# Revit family: LEGRAND_NON INTERLOCKED SOCKETS_SURFACE MOUNTED_IP44_440
name_source: partatom
category: Installations électriques
revit_build: Autodesk Revit 2018 (Build: 20170223_1515(x64)
units: mm (PartAtom-declared; Revit-internal decimal feet)

## family parameters
Conserver l'orientation des annotations = Non
Cote de connecteur circulaire = Utiliser le diamètre
Couper avec des vides une fois chargée = Non
Hôte = Face
Partagée = Non
Point de calcul de pièce = Non
Type d'élément = Normal

## types (6) — shared parameters
Description = international standard socket for flush or surface mounting with accessory allows the connection of power devices
Dia bouchon = 50 mm  [stored 0.164042 ft]
Elévation par défaut = 1000 mm  [stored 3.28084 ft]
Fabricant = Legrand
Flush E or Surface mounting S = flush and surface mounting
General Conditions of Use = https://export.legrand.com
Maximum installation temperature = 40°C
Maximum use temperature = 100°C
Minimum installation temperature = -20°C
Minimum use temperature = -50°C
Number of poles = 4
RAY BOUCHON = 25 mm  [stored 0.082021 ft]
Ray = 25 mm  [stored 0.082021 ft]
Standard IEC or NFC = IEC
Tension V = 400 440 V  50 60 Hz red
characteristic color = red
connecting type = screw terminals
material of box = plastic
resistance to chocks IK = 09
vertical fixing distance mm = 70 mm

## per-type parameters (varying)
| type | Modèle | Position of earth h | depth for flush mounting mm | depth mm | h1 | halogen free | height mm | horizontal fixing distance mm | intensity A | protection class IP | width mm |
| panel mounting socket Hypra   IP 44   ELV 16 A   440/460 V   2P+E   plast surface box for passage wiring | 052310 | 11 | 75 mm | 115 mm | 109 mm | Oui | 182 mm | 60 mm | 16 A | IP44 | 86 mm |
| panel mounting socket à single fixing center Hypra   IP44   32 A   440/460 V   3P+E   plast surface mounting | 052350 | 11 | 90 mm  [stored 0.295276 ft] | 139 mm | 97 mm | Oui | 162 mm | 70 mm | 32 A | IP44 | 102 mm |
| panel mounting socket single fixing center Hypra IP66/67-55 32A 440V conteneur frigo 3P+E plast surface mounting | 052926 | 3 | 90 mm  [stored 0.295276 ft] | 140 mm  [stored 0.459318 ft] | 97 mm | Non | 162 mm | 70 mm | 32 A | IP66/67-55 | 102 mm |
| panel mounting socket Hypra   IP44   ELV 16 A   440/460 V   2P+E   plast surface mounting | 052310 | 11 | 58 mm | 98 mm | 64 mm  [stored 0.209974 ft] | Oui | 106 mm | 60 mm | 16 A | IP44 | 74 mm |
| panel mounting socket à single fixing center Hypra   IP 44   32 A   440 460 V   3P+T   plast surface box for passage wiring | 052350 | 11 | 90 mm  [stored 0.295276 ft] | 139 mm | 97 mm | Oui | 162 mm | 70 mm | 32 A | IP44 | 102 mm |
| panel mounting socket single fixing center Hypra IP66/67-55 32A 440V conteneur frigo 3P+E plast surface box for passage wiring | 052926 | 3 | 90 mm  [stored 0.295276 ft] | 140 mm  [stored 0.459318 ft] | 97 mm | Non | 162 mm | 70 mm | 32 A | IP66/67-55 | 102 mm |

note: [stored X ft] marks values corroborated as IEEE doubles in the binary element streams (Revit-internal decimal feet)
